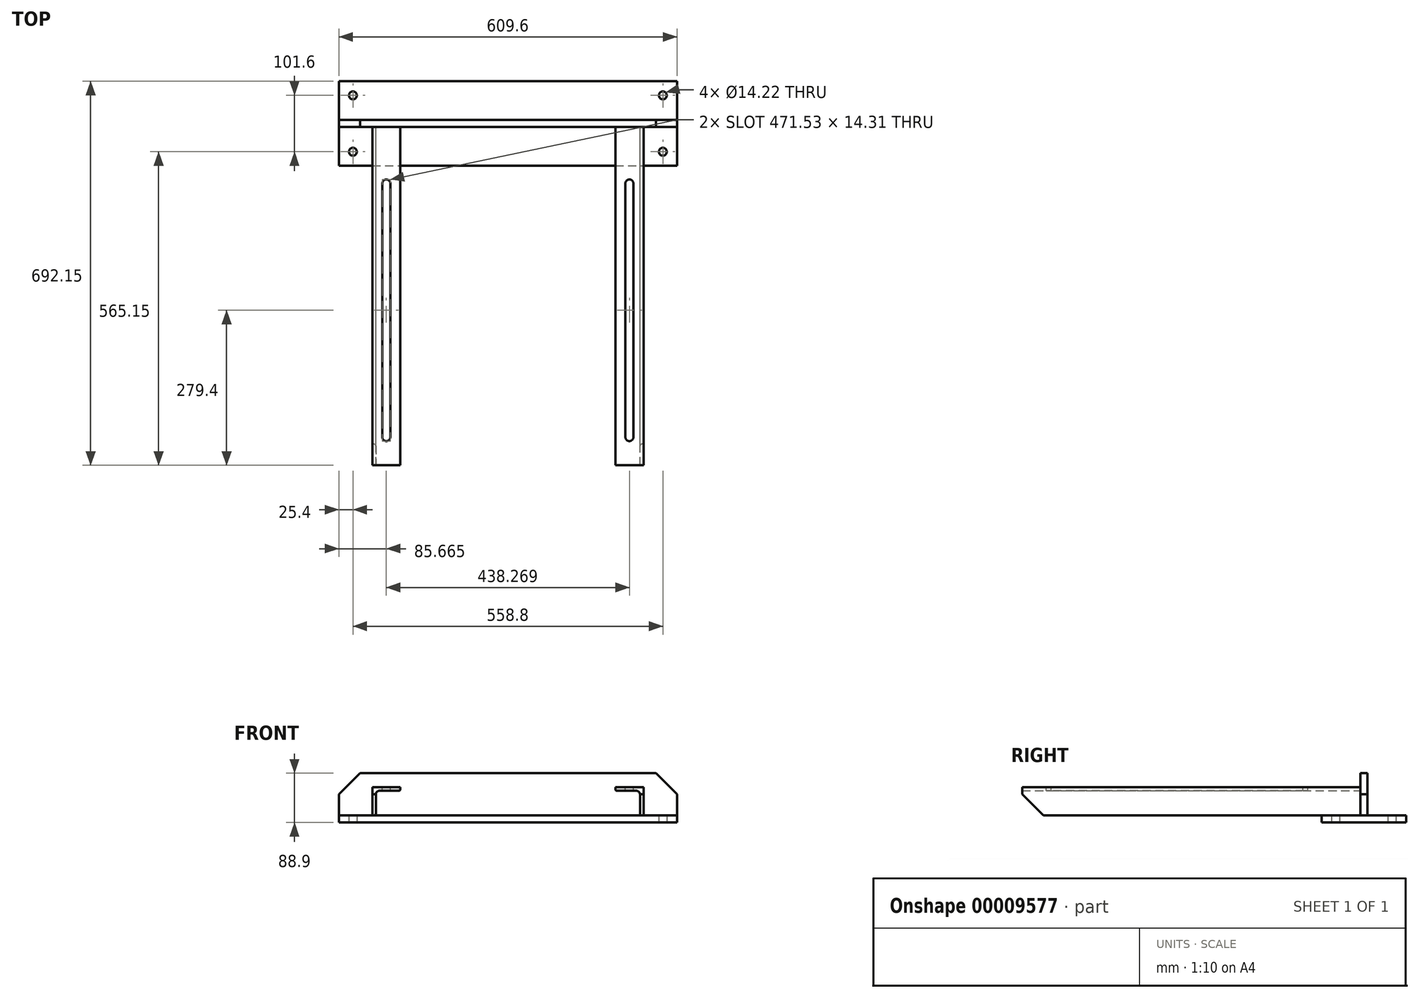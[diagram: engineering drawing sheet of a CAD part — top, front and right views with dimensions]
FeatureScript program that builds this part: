
annotation { "Feature Type Name" : "Feature", "Feature Type Description" : "" }
export const myFeature = defineFeature(function(context is Context, id is Id, definition is map)
    precondition{}
    {
        {
            var Q0;
            Q0=qCreatedBy(makeId("Top.planeOp"),FACE);
            var sketch = newSketch(context, id + "F0", { "sketchPlane" : qUnion([Q0])});
            skLineSegment(sketch, "E0.rect.bottom", {"start": v(-304.8, 76.2) * mm, "end": v(304.8, 76.2) * mm});
            skLineSegment(sketch, "E0.rect.top", {"start": v(-304.8, -76.2) * mm, "end": v(304.8, -76.2) * mm});
            skLineSegment(sketch, "E0.rect.left", {"start": v(-304.8, 76.2) * mm, "end": v(-304.8, -76.2) * mm});
            skLineSegment(sketch, "E0.rect.right", {"start": v(304.8, 76.2) * mm, "end": v(304.8, -76.2) * mm});
            skPoint(sketch, "E0.rect.middle", {"position": v(0, 0) * mm});
            skLineSegment(sketch, "E1", {"start": v(0, 76.2) * mm, "end": v(0, -76.2) * mm, "construction": true});
            skLineSegment(sketch, "E2", {"start": v(-304.8, 0) * mm, "end": v(304.8, 0) * mm, "construction": true});
            skLineSegment(sketch, "E3.0", {"start": v(-304.8, -50.8) * mm, "end": v(304.8, -50.8) * mm, "construction": true});
            skLineSegment(sketch, "E4.0", {"start": v(-279.4, 76.2) * mm, "end": v(-279.4, -76.2) * mm, "construction": true});
            skCircle(sketch, "E5", {"center": v(-279.4, -50.8) * mm, "radius": 7.11 * mm});
            skCircle(sketch, "E6.0.MirrorC", {"center": v(-279.4, 50.8) * mm, "radius": 7.11 * mm});
            skCircle(sketch, "E7.0.MirrorC", {"center": v(279.4, 50.8) * mm, "radius": 7.11 * mm});
            skCircle(sketch, "E8.0.MirrorC", {"center": v(279.4, -50.8) * mm, "radius": 7.11 * mm});
            skSolve(sketch);
        }
        {
            var Q0;
            Q0=makeQuery(id+"F0.imprint","IMPRINT",FACE,{"disambiguationData":[TD([[makeQuery(id+"F0.imprint","IMPRINT",EDGE,{"derivedFrom":sQuery(id+"F0.wireOp",EDGE,"E0.rect.bottom")}),-1.0]])]});
            extrude(context, id + "F1", {"entities" : qUnion([Q0]), "depth" : 12.7 * mm});
        }
        {
            var Q0;
            Q0=makeQuery(id+"F1.opExtrude","CAP_FACE",FACE,{"disambiguationData":[OSD([sQuery(id+"F0.wireOp",EDGE,"E0.rect.bottom"),sQuery(id+"F0.wireOp",EDGE,"E0.rect.top"),sQuery(id+"F0.wireOp",EDGE,"E0.rect.left"),sQuery(id+"F0.wireOp",EDGE,"E0.rect.right"),sQuery(id+"F0.wireOp",EDGE,"E5"),sQuery(id+"F0.wireOp",EDGE,"E6.0.MirrorC"),sQuery(id+"F0.wireOp",EDGE,"E7.0.MirrorC"),sQuery(id+"F0.wireOp",EDGE,"E8.0.MirrorC")])],"isStart":false});
            var sketch = newSketch(context, id + "F2", { "sketchPlane" : qUnion([Q0])});
            skLineSegment(sketch, "E9", {"start": v(-304.8, 0) * mm, "end": v(304.8, 0) * mm, "construction": true});
            skLineSegment(sketch, "E10.0", {"start": v(-304.8, -6.35) * mm, "end": v(304.8, -6.35) * mm});
            skLineSegment(sketch, "E11.0.MirrorCS", {"start": v(-304.8, 6.35) * mm, "end": v(304.8, 6.35) * mm});
            skLineSegment(sketch, "E12", {"start": v(-304.8, 6.35) * mm, "end": v(-304.8, -6.35) * mm});
            skLineSegment(sketch, "E13", {"start": v(304.8, 6.35) * mm, "end": v(304.8, -6.35) * mm});
            skSolve(sketch);
        }
        {
            var Q0;
            Q0 = qSketchRegion(id + "F2", true);
            extrude(context, id + "F3", {"entities" : qUnion([Q0]), "depth" : 76.2 * mm});
        }
        {
            var Q0;
            Q0=makeQuery(id+"F3.opExtrude","CAP_EDGE",EDGE,{"disambiguationData":[OSD([sQuery(id+"F2.wireOp",EDGE,"E13")])],"isStart":false});
            var Q1;
            Q1=makeQuery(id+"F3.opExtrude","CAP_EDGE",EDGE,{"disambiguationData":[OSD([sQuery(id+"F2.wireOp",EDGE,"E12")])],"isStart":false});
            chamfer(context, id + "F4", {"entities" : qUnion([Q0, Q1]), "width" : 38.1 * mm, "tangentPropagation" : true});
        }
        {
            var Q0;
            Q0=makeQuery(id+"F3.opExtrude","SWEPT_FACE",FACE,{"disambiguationData":[OSD([sQuery(id+"F2.wireOp",EDGE,"E10.0")])]});
            var sketch = newSketch(context, id + "F5", { "sketchPlane" : qUnion([Q0])});
            skLineSegment(sketch, "E14", {"start": v(0, 88.9) * mm, "end": v(0, -133.62) * mm, "construction": true});
            skLineSegment(sketch, "E15.0", {"start": v(-244.48, 63.5) * mm, "end": v(-244.48, 12.7) * mm});
            skLineSegment(sketch, "E16.0", {"start": v(-244.48, 12.7) * mm, "end": v(-241.3, 12.7) * mm});
            skLineSegment(sketch, "E17.0", {"start": v(-238.13, 50.8) * mm, "end": v(-238.13, 15.88) * mm});
            skLineSegment(sketch, "E18.0", {"start": v(-193.68, 63.5) * mm, "end": v(-193.68, 60.33) * mm});
            skLineSegment(sketch, "E19.0", {"start": v(-244.48, 63.5) * mm, "end": v(-193.68, 63.5) * mm});
            skLineSegment(sketch, "E20.0", {"start": v(-231.78, 57.15) * mm, "end": v(-196.85, 57.15) * mm});
            skLineSegment(sketch, "E21.trimOffspring", {"start": v(0, 12.7) * mm, "end": v(304.8, 12.7) * mm});
            skPoint(sketch, "E22.orphan", {"position": v(-304.8, 12.7) * mm});
            skPoint(sketch, "E23.visualSharp", {"position": v(-238.13, 57.15) * mm});
            skArc(sketch, "E23.filletArc", {"start": v(-231.78, 57.15) * mm, "mid": v(-236.27, 55.3) * mm, "end": v(-238.13, 50.8) * mm});
            skPoint(sketch, "E24.visualSharp", {"position": v(-193.68, 57.15) * mm});
            skArc(sketch, "E24.filletArc", {"start": v(-196.85, 57.15) * mm, "mid": v(-194.6, 58.08) * mm, "end": v(-193.68, 60.33) * mm});
            skPoint(sketch, "E25.visualSharp", {"position": v(-238.13, 12.7) * mm});
            skArc(sketch, "E25.filletArc", {"start": v(-241.3, 12.7) * mm, "mid": v(-239.05, 13.63) * mm, "end": v(-238.12, 15.88) * mm});
            skSolve(sketch);
        }
        {
            var Q0;
            Q0 = qSketchRegion(id + "F5", true);
            extrude(context, id + "F6", {"entities" : qUnion([Q0]), "depth" : 609.6 * mm});
        }
        {
            var Q0;
            Q0=makeQuery(id+"F6.opExtrude","SWEPT_FACE",FACE,{"disambiguationData":[OSD([sQuery(id+"F5.wireOp",EDGE,"E19.0")])]});
            var sketch = newSketch(context, id + "F7", { "sketchPlane" : qUnion([Q0])});
            skArc(sketch, "E26.0", {"start": v(-226.3, -565.15) * mm, "mid": v(-218.2, -572.31) * mm, "end": v(-212.07, -563.43) * mm});
            skLineSegment(sketch, "E27", {"start": v(-282.34, -336.55) * mm, "end": v(-392.5, -336.55) * mm, "construction": true});
            skArc(sketch, "E28.0.MirrorC", {"start": v(-226.3, -107.95) * mm, "mid": v(-218.2, -100.79) * mm, "end": v(-212.07, -109.67) * mm});
            skPoint(sketch, "E29.0.3.end.orphan", {"position": v(117.36, -335.5) * mm});
            skPoint(sketch, "E29.0.2.end.orphan", {"position": v(117.36, -623.5) * mm});
            skPoint(sketch, "E29.0.1.end.orphan", {"position": v(-314.66, -623.5) * mm});
            skPoint(sketch, "E29.0.1.start.orphan", {"position": v(-314.66, -335.5) * mm});
            skLineSegment(sketch, "E30", {"start": v(-226.3, -107.95) * mm, "end": v(-226.3, -565.15) * mm});
            skLineSegment(sketch, "E31", {"start": v(-212.07, -563.43) * mm, "end": v(-212.07, -109.67) * mm});
            skLineSegment(sketch, "E32", {"start": v(-219.08, -615.95) * mm, "end": v(-219.08, -19.45) * mm, "construction": true});
            skSolve(sketch);
        }
        {
            var Q0;
            Q0 = qSketchRegion(id + "F7", true);
            extrude(context, id + "F8", {"entities" : qUnion([Q0]), "operationType" : NewBodyOperationType.REMOVE, "endBound" : BoundingType.THROUGH_ALL, "oppositeDirection" : true, "depth" : 25.4 * mm});
        }
        {
            var Q0;
            Q0=makeQuery(id+"F6.opExtrude","SWEPT_BODY",BODY,{"disambiguationData":[OSD([sQuery(id+"F5.wireOp",EDGE,"E15.0"),sQuery(id+"F5.wireOp",EDGE,"E16.0"),sQuery(id+"F5.wireOp",EDGE,"E17.0"),sQuery(id+"F5.wireOp",EDGE,"E18.0"),sQuery(id+"F5.wireOp",EDGE,"E19.0"),sQuery(id+"F5.wireOp",EDGE,"E20.0"),sQuery(id+"F5.wireOp",EDGE,"E23.filletArc"),sQuery(id+"F5.wireOp",EDGE,"E24.filletArc"),sQuery(id+"F5.wireOp",EDGE,"E25.filletArc")])]});
            var Q1;
            Q1=qCreatedBy(makeId("Right.planeOp"),FACE);
            mirror(context, id + "F9", {"entities" : qUnion([Q0]), "mirrorPlane" : qUnion([Q1])});
        }
        {
            var Q0;
            Q0=makeQuery(id+"F6.opExtrude","SWEPT_FACE",FACE,{"disambiguationData":[OSD([sQuery(id+"F5.wireOp",EDGE,"E15.0")])]});
            var sketch = newSketch(context, id + "F10", { "sketchPlane" : qUnion([Q0])});
            skLineSegment(sketch, "E33.0", {"start": v(615.95, 63.5) * mm, "end": v(615.95, 12.7) * mm, "construction": true});
            skLineSegment(sketch, "E34.0", {"start": v(615.95, 12.7) * mm, "end": v(6.35, 12.7) * mm, "construction": true});
            skLineSegment(sketch, "E35.0", {"start": v(577.85, 63.5) * mm, "end": v(577.85, 12.7) * mm, "construction": true});
            skLineSegment(sketch, "E36.0", {"start": v(615.95, 50.8) * mm, "end": v(6.35, 50.8) * mm, "construction": true});
            skLineSegment(sketch, "E37", {"start": v(615.95, 50.8) * mm, "end": v(577.85, 12.7) * mm});
            skLineSegment(sketch, "E38", {"start": v(615.95, 50.8) * mm, "end": v(615.95, 12.7) * mm});
            skLineSegment(sketch, "E39", {"start": v(615.95, 12.7) * mm, "end": v(577.85, 12.7) * mm});
            skSolve(sketch);
        }
        {
            var Q0;
            Q0 = qSketchRegion(id + "F10", true);
            extrude(context, id + "F11", {"entities" : qUnion([Q0]), "operationType" : NewBodyOperationType.REMOVE, "endBound" : BoundingType.THROUGH_ALL, "oppositeDirection" : true, "depth" : 25.4 * mm});
        }
    });
